# Revit family: Column-Steel-UB Universal Beam-Steel & Tube-350 S0 (seismic)_
name_source: partatom
category: Structural Columns
revit_build: Autodesk Revit 2017 (Build: 20170118_1100(x64)
units: mm (PartAtom-declared; Revit-internal decimal feet)

## family parameters
Always export as geometry = No
Beam cutback in plan = From geometry
Cut with Voids When Loaded = No
Material for Model Behavior = Steel
OmniClass Number = 23.25.30.11.14.11
OmniClass Title = Columns
Section Shape = I-shape Parallel Flange
Shared = No
Show family pre-cut in plan views = Yes

## types (1)
- 410UB59.7 S0
    Assembly Code = B1010250
    CBICode = 3421
    CBIDescription = Light steel framing
    Centre Horizontal = 89 mm  [stored 0.291995 ft]
    Centroid Horizontal = 89.0 mm
    Centroid Vertical = 203.0 mm
    Clear Web Height = 383.2 mm
    Description = Steel & Tube supplies a full range of hot rolled seismic and non seismic universal beams, columns, plate and channels. For more information please refer to the Design with Steel product catalogue on our website.
    Design Instruction = Design information should be cross referenced with the Steel & Tube Design with Steel Design Guide and NZS 3404: Part1: 2009
    Design Standard = NZS 3404: Part 1: 2009 including reference to the NZBC
    Elastic Modulus strong axis = 135000.0 mm³
    Elastic Modulus weak axis = 1060000.0 mm³
    Flange Thickness = 12.8 mm
    Flange Toe of Fillet = 17.8 mm
    Form Factor = 0.918
    Height = 406.0 mm
    Manufactured Standard = AS/NZS 3679.1: 2016
    Manufacturer = Steel & Tube
    ManufacturerName = Steel & Tube
    ManufacturerURL = http://www.steelandtube.co.nz
    MassPerUnitLength_ANZRS = 59.70 kg/m
    MaximumLength_ANZRS = 18000 mm
    Model = 410UB59.7 S0
    ModifiedIssue_ANZRS = 20160330 $
    Moment of Inertia strong axis = 12100000.00 mm4
    Moment of Inertia weak axis = 216000000.00 mm4
    Nominal Weight = 59.70 kgf/m
    Perimeter = 1.49 m²/m
    Plastic Modulus strong axis = 209000.0 mm³
    Plastic Modulus weak axis = 1200000.0 mm³
    Principal Axes Angle = 90.00°
    Section Area = 7640.0 mm²
    Section Name Key = UB 410x59.7
    SectionAreaGross_ANZRS = 7640.0 mm²
    SectionAreaNet_ANZRS = 7640.0 mm²
    Shear Area strong axis = 7640.0 mm²
    Shear Area weak axis = 7640.0 mm²
    Tensile Strength = 480.0 MPa
    Torsional Modulus = 0.0 mm³
    Torsional Moment of Inertia = 337000.00 mm4
    Type Comments = New Zealand Steel Structures Standard NZS 3404: part 1:2009 clause 2.2.4. (Steel for Seismic Applications) Refer table 1, 2 and 4
    URL = http://www.steelandtube.co.nz
    Uniclass2015Code = Pr_20_76_51_12
    Uniclass2015Title = Carbon steel beams, columns, channels and tees
    Uniclass2015Version = 2015
    Warping Constant = 467000000000.0 mm6
    Web Fillet = 11.4 mm
    Web Thickness = 12.8 mm
    Web Toe of Fillet = 71.2 mm
    Width = 178.0 mm
    X-Compactness = C
    X-Zex = 1200000.0 mm³
    Y-Compactness = C
    Y-Zey = 203000.0 mm³
    Yield Stress Flange = 340.0 MPa
    Yield Stress Web = 360.0 MPa

note: [stored X ft] marks values corroborated as IEEE doubles in the binary element streams (Revit-internal decimal feet)

## geometry (parser evidence)
native form markers: Sweep x4
no freeform markers — native parametric forms only
